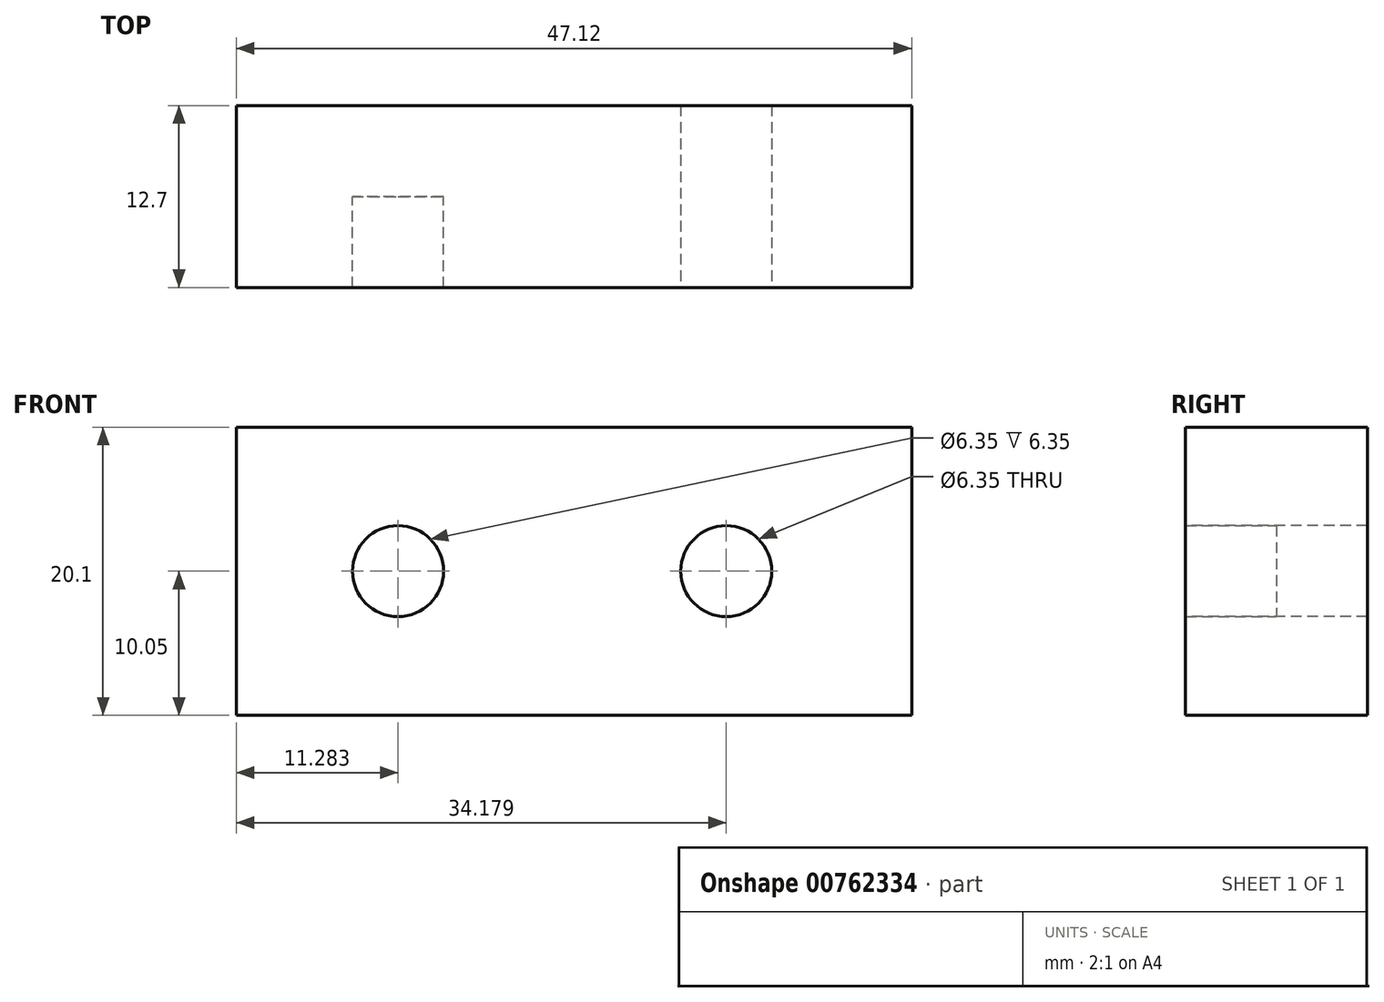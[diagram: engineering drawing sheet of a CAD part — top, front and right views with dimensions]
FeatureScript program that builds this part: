
annotation { "Feature Type Name" : "Feature", "Feature Type Description" : "" }
export const myFeature = defineFeature(function(context is Context, id is Id, definition is map)
    precondition{}
    {
        {
            var Q0;
            Q0=qCreatedBy(makeId("Front.planeOp"),FACE);
            var sketch = newSketch(context, id + "F0", { "sketchPlane" : qUnion([Q0])});
            skLineSegment(sketch, "E0.bottom", {"start": v(23.56, -10.05) * mm, "end": v(-23.56, -10.05) * mm});
            skLineSegment(sketch, "E0.top", {"start": v(23.56, 10.05) * mm, "end": v(-23.56, 10.05) * mm});
            skLineSegment(sketch, "E0.left", {"start": v(23.56, -10.05) * mm, "end": v(23.56, 10.05) * mm});
            skLineSegment(sketch, "E0.right", {"start": v(-23.56, -10.05) * mm, "end": v(-23.56, 10.05) * mm});
            skPoint(sketch, "E0.middle", {"position": v(0, 0) * mm});
            skPoint(sketch, "E1", {"position": v(-12.28, 0) * mm});
            skSolve(sketch);
        }
        {
            var Q0;
            Q0 = qSketchRegion(id + "F0", true);
            extrude(context, id + "F1", {"entities" : qUnion([Q0]), "endBound" : BoundingType.SYMMETRIC, "depth" : 12.7 * mm, "offsetDistance" : 25.4 * mm});
        }
        {
            var Q0;
            Q0=sQuery(id+"F0.wireOp",VERTEX,"E1");
            var Q1;
            Q1=makeQuery(id+"F1.opExtrude","SWEPT_BODY",BODY,{"disambiguationData":[OSD([sQuery(id+"F0.wireOp",EDGE,"E0.bottom"),sQuery(id+"F0.wireOp",EDGE,"E0.top"),sQuery(id+"F0.wireOp",EDGE,"E0.left"),sQuery(id+"F0.wireOp",EDGE,"E0.right")])]});
            hole(context, id + "F2", {"style" : HoleStyle.SIMPLE, "endStyle" : HoleEndStyle.THROUGH, "oppositeDirection" : true, "holeDiameter" : 6.35 * mm, "majorDiameter" : 6.35 * mm, "isTappedThrough" : true, "tappedDepth" : 12.7 * mm, "tapClearance" : 3, "locations" : qUnion([Q0]), "scope" : qUnion([Q1])});
        }
        {
            var Q0;
            Q0=makeQuery(id+"F1.opExtrude","CAP_FACE",FACE,{"disambiguationData":[OSD([sQuery(id+"F0.wireOp",EDGE,"E0.bottom"),sQuery(id+"F0.wireOp",EDGE,"E0.top"),sQuery(id+"F0.wireOp",EDGE,"E0.left"),sQuery(id+"F0.wireOp",EDGE,"E0.right")])],"isStart":false});
            var sketch = newSketch(context, id + "F3", { "sketchPlane" : qUnion([Q0])});
            skPoint(sketch, "E2", {"position": v(10.62, 0) * mm});
            skPoint(sketch, "E2.positionSnap0", {"position": v(23.56, 0) * mm});
            skSolve(sketch);
        }
        {
            var Q0;
            Q0=sQuery(id+"F3.wireOp",VERTEX,"E2");
            var Q1;
            Q1=makeQuery(id+"F1.opExtrude","SWEPT_BODY",BODY,{"disambiguationData":[OSD([sQuery(id+"F0.wireOp",EDGE,"E0.bottom"),sQuery(id+"F0.wireOp",EDGE,"E0.top"),sQuery(id+"F0.wireOp",EDGE,"E0.left"),sQuery(id+"F0.wireOp",EDGE,"E0.right")])]});
            hole(context, id + "F4", {"style" : HoleStyle.SIMPLE, "endStyle" : HoleEndStyle.THROUGH, "holeDiameter" : 6.35 * mm, "majorDiameter" : 6.35 * mm, "isTappedThrough" : true, "tappedDepth" : 12.7 * mm, "tapClearance" : 3, "locations" : qUnion([Q0]), "scope" : qUnion([Q1])});
        }
    });
